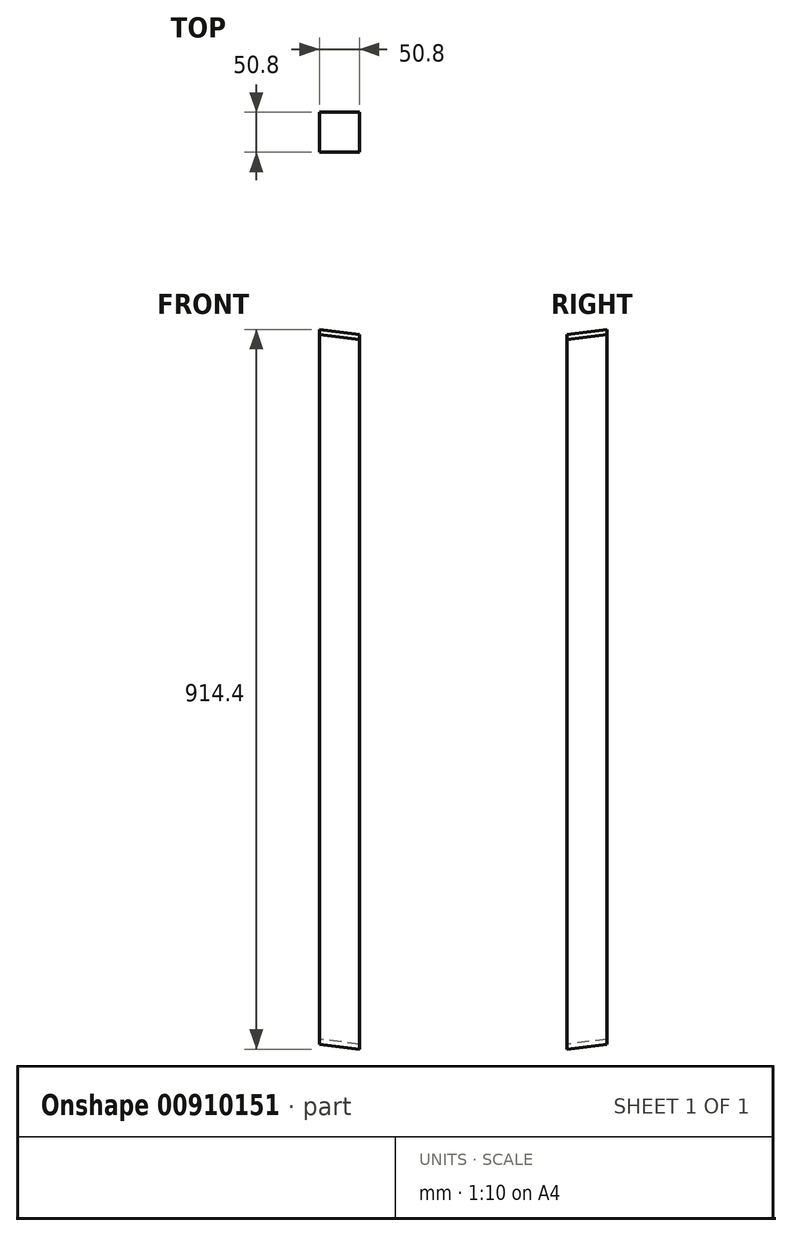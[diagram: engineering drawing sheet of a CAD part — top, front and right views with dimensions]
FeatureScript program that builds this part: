
annotation { "Feature Type Name" : "Feature", "Feature Type Description" : "" }
export const myFeature = defineFeature(function(context is Context, id is Id, definition is map)
    precondition{}
    {
        {
            var Q0;
            Q0=qCreatedBy(makeId("Front.planeOp"),FACE);
            var Q1;
            Q1=qCreatedBy(makeId("Right.planeOp"),FACE);
            cPlane(context, id + "F0", {"entities" : qUnion([Q0, Q1]), "cplaneType" : CPlaneType.MID_PLANE, "offset" : 25.4 * mm, "width" : 152.4 * mm, "height" : 152.4 * mm});
        }
        {
            var Q0;
            Q0=qCreatedBy(makeId("Right.planeOp"),FACE);
            var sketch = newSketch(context, id + "F1", { "sketchPlane" : qUnion([Q0])});
            skLineSegment(sketch, "E0.bottom", {"start": v(0, 0) * mm, "end": v(-50.8, 0) * mm});
            skLineSegment(sketch, "E0.top", {"start": v(0, 914.4) * mm, "end": v(-50.8, 914.4) * mm});
            skLineSegment(sketch, "E0.left", {"start": v(0, 0) * mm, "end": v(0, 914.4) * mm});
            skLineSegment(sketch, "E0.right", {"start": v(-50.8, 0) * mm, "end": v(-50.8, 914.4) * mm});
            skSolve(sketch);
        }
        {
            var Q0;
            Q0 = qSketchRegion(id + "F1", true);
            extrude(context, id + "F2", {"entities" : qUnion([Q0]), "depth" : 50.8 * mm, "offsetDistance" : 25.4 * mm});
        }
        {
            var Q0;
            Q0=qCreatedBy(id+"F0.planeOp",FACE);
            var sketch = newSketch(context, id + "F3", { "sketchPlane" : qUnion([Q0])});
            skLineSegment(sketch, "E1", {"start": v(0, 914.4) * mm, "end": v(71.84, 914.4) * mm});
            skLineSegment(sketch, "E2", {"start": v(71.84, 914.4) * mm, "end": v(71.84, 901.73) * mm});
            skLineSegment(sketch, "E3", {"start": v(71.84, 901.73) * mm, "end": v(0, 914.4) * mm});
            skSolve(sketch);
        }
        {
            var Q0;
            Q0 = qSketchRegion(id + "F3", true);
            extrude(context, id + "F4", {"entities" : qUnion([Q0]), "operationType" : NewBodyOperationType.REMOVE, "endBound" : BoundingType.SYMMETRIC, "oppositeDirection" : true, "depth" : 76.2 * mm, "offsetDistance" : 25.4 * mm});
        }
        {
            var Q0;
            Q0=qCreatedBy(id+"F0.planeOp",FACE);
            var sketch = newSketch(context, id + "F5", { "sketchPlane" : qUnion([Q0])});
            skLineSegment(sketch, "E4", {"start": v(0, 0) * mm, "end": v(71.84, 0) * mm});
            skLineSegment(sketch, "E5", {"start": v(0, 12.67) * mm, "end": v(0, 0) * mm});
            skLineSegment(sketch, "E6", {"start": v(71.84, 0) * mm, "end": v(0, 12.67) * mm});
            skSolve(sketch);
        }
        {
            var Q0;
            Q0 = qSketchRegion(id + "F5", true);
            extrude(context, id + "F6", {"entities" : qUnion([Q0]), "operationType" : NewBodyOperationType.REMOVE, "endBound" : BoundingType.SYMMETRIC, "oppositeDirection" : true, "depth" : 76.2 * mm, "offsetDistance" : 25.4 * mm});
        }
    });
